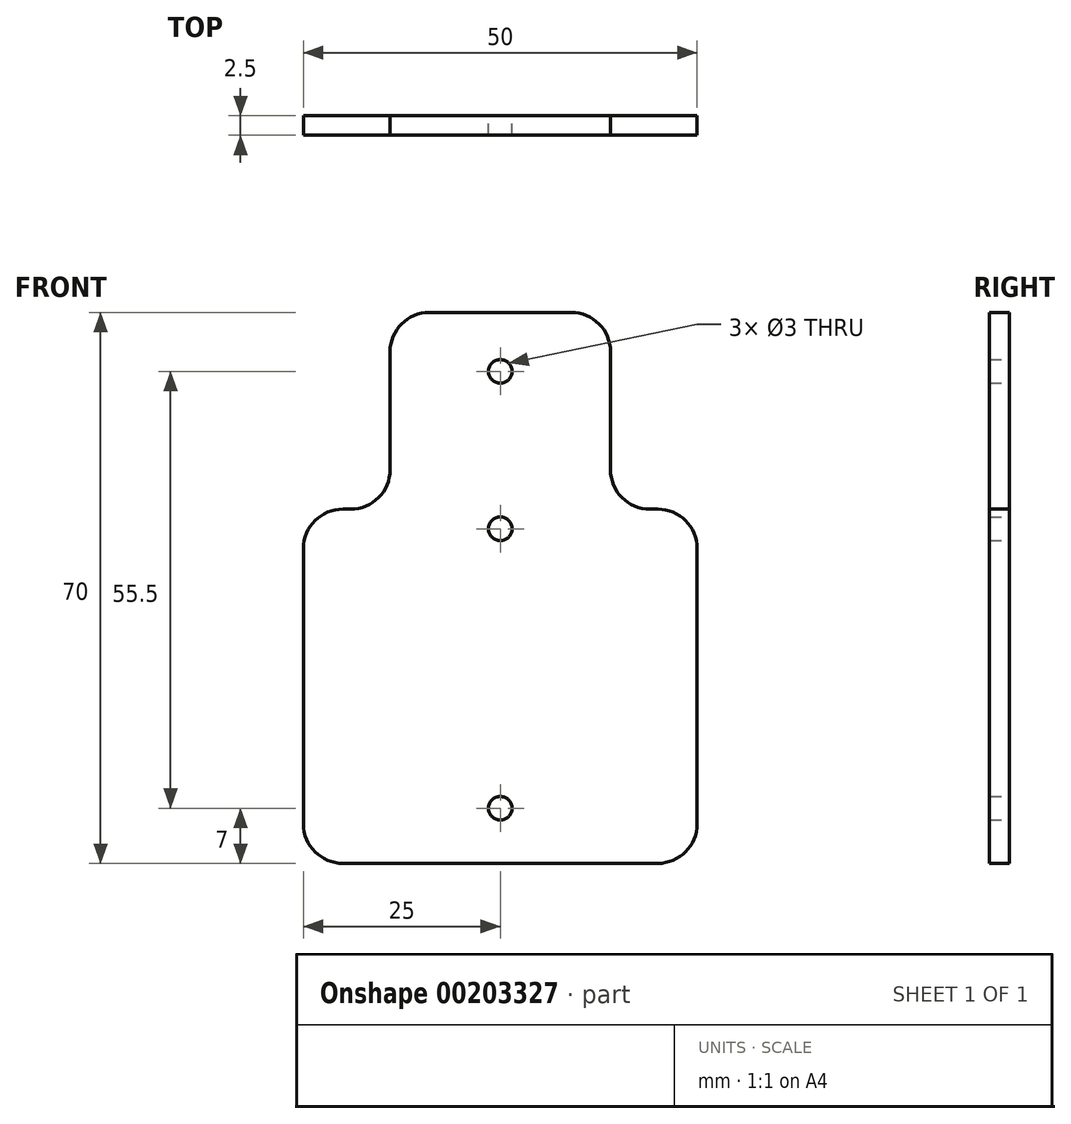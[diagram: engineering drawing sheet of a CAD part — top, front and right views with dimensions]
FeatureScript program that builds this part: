
annotation { "Feature Type Name" : "Feature", "Feature Type Description" : "" }
export const myFeature = defineFeature(function(context is Context, id is Id, definition is map)
    precondition{}
    {
        {
            var Q0;
            Q0=qCreatedBy(makeId("Front.planeOp"),FACE);
            var sketch = newSketch(context, id + "F0", { "sketchPlane" : qUnion([Q0])});
            skLineSegment(sketch, "E0.top", {"start": v(14, 35) * mm, "end": v(-14, 35) * mm});
            skPoint(sketch, "E0.middle", {"position": v(0, 0) * mm});
            skLineSegment(sketch, "E1", {"start": v(0, 35) * mm, "end": v(0, -35) * mm, "construction": true});
            skCircle(sketch, "E2", {"center": v(0, 27.5) * mm, "radius": 1.5 * mm});
            skCircle(sketch, "E3", {"center": v(0, 7.5) * mm, "radius": 1.5 * mm});
            skLineSegment(sketch, "E4.bottom", {"start": v(-25, -35) * mm, "end": v(25, -35) * mm});
            skLineSegment(sketch, "E4.top", {"start": v(-25, 10) * mm, "end": v(-14, 10) * mm});
            skLineSegment(sketch, "E4.left", {"start": v(-25, -35) * mm, "end": v(-25, 10) * mm});
            skLineSegment(sketch, "E4.right", {"start": v(25, -35) * mm, "end": v(25, 10) * mm});
            skLineSegment(sketch, "E5", {"start": v(-14, 35) * mm, "end": v(-14, 10) * mm});
            skLineSegment(sketch, "E6", {"start": v(14, 35) * mm, "end": v(14, 10) * mm});
            skLineSegment(sketch, "E7.trimOffspring", {"start": v(14, 10) * mm, "end": v(25, 10) * mm});
            skCircle(sketch, "E8", {"center": v(0, -28) * mm, "radius": 1.5 * mm});
            skSolve(sketch);
        }
        {
            var Q0;
            Q0 = qSketchRegion(id + "F0", true);
            extrude(context, id + "F1", {"entities" : qUnion([Q0]), "depth" : 2.5 * mm});
        }
        {
            var Q0;
            Q0=makeQuery(id+"F1.opExtrude","SWEPT_EDGE",EDGE,{"disambiguationData":[OSD([sQuery(id+"F0.wireOp",EDGE,"E0.top"),sQuery(id+"F0.wireOp",EDGE,"2655a029-c715-4d3c-892c-dbc03d8aa715")])]});
            var Q1;
            Q1=makeQuery(id+"F1.opExtrude","SWEPT_EDGE",EDGE,{"disambiguationData":[OSD([sQuery(id+"F0.wireOp",EDGE,"E0.top"),sQuery(id+"F0.wireOp",EDGE,"3bb541ac-b7ac-42df-8648-389a798b144d0.MirrorCS")])]});
            var Q2;
            Q2=makeQuery(id+"F1.opExtrude","SWEPT_EDGE",EDGE,{"disambiguationData":[OSD([sQuery(id+"F0.wireOp",EDGE,"E4.top"),sQuery(id+"F0.wireOp",EDGE,"E5")])]});
            var Q3;
            Q3=makeQuery(id+"F1.opExtrude","SWEPT_EDGE",EDGE,{"disambiguationData":[OSD([sQuery(id+"F0.wireOp",EDGE,"E4.top"),sQuery(id+"F0.wireOp",EDGE,"E4.left")])]});
            var Q4;
            Q4=makeQuery(id+"F1.opExtrude","SWEPT_EDGE",EDGE,{"disambiguationData":[OSD([sQuery(id+"F0.wireOp",EDGE,"E6"),sQuery(id+"F0.wireOp",EDGE,"E7.trimOffspring")])]});
            var Q5;
            Q5=makeQuery(id+"F1.opExtrude","SWEPT_EDGE",EDGE,{"disambiguationData":[OSD([sQuery(id+"F0.wireOp",EDGE,"E4.right"),sQuery(id+"F0.wireOp",EDGE,"E7.trimOffspring")])]});
            var Q6;
            Q6=makeQuery(id+"F1.opExtrude","SWEPT_EDGE",EDGE,{"disambiguationData":[OSD([sQuery(id+"F0.wireOp",EDGE,"E4.bottom"),sQuery(id+"F0.wireOp",EDGE,"E4.left")])]});
            var Q7;
            Q7=makeQuery(id+"F1.opExtrude","SWEPT_EDGE",EDGE,{"disambiguationData":[OSD([sQuery(id+"F0.wireOp",EDGE,"E4.bottom"),sQuery(id+"F0.wireOp",EDGE,"E4.right")])]});
            fillet(context, id + "F2", {"entities" : qUnion([Q0, Q1, Q2, Q3, Q4, Q5, Q6, Q7]), "radius" : 5 * mm, "tangentPropagation" : true, "allowEdgeOverflow" : false});
        }
    });
